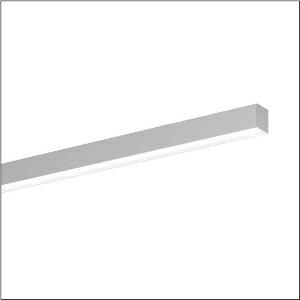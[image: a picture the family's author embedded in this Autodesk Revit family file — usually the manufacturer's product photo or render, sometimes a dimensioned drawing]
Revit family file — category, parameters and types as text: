
# Revit family: silica_r__21_51mx23db35sb_5652
name_source: partatom
category: Lighting Fixtures
units: mm (PartAtom-declared; Revit-internal decimal feet)

## family parameters
Cut with Voids When Loaded = No
Host = Face
Light Source = No
Part Type = Normal
Room Calculation Point = No
Round Connector Dimension = Use Diameter
Shared = No

## types (1)
- --- (1 x LED, 4100 lm, 30.1 W, 3000K)
    Apparent Load = 30 VA
    CIE Flux Codes = 78 96 99 100 100
    Color Rendering = 80
    Color Temperature = 3000K
    Default Elevation = 1800 mm
    Description = Silica® 21, office luminaire, primary optical cover: prismatic diffuser, of PMMA, CAT 2 (L<= 3000cd/m²), light emission: direct distribution, primary light characteristic: symmetric, installation type: surface-mounted, LED, rated luminous flux: 4.100lm, luminous efficacy: 136lm/W, light colour: 830, colour temperature: 3000K, with terminal, 3+2-pole, max. 2.5mm², mains connection: 220..240V, AC, 50/60Hz, rated input power: 30.1W, luminaire housing, of aluminium, metallic grey (RAL 9006), length: 1.504mm, width: 53mm, height: 53mm, protection rating (complete): IP20, insulation class (complete): insulation class I (protective earthing), certification: CE, permissible operating ambient temperature: 0..+35°C, standard: EN 50419, packaging unit: 1 piece
    Height = 0 mm  [stored 0 ft]
    Lamp = 1 x LED
    Lamp Light Flux = 4100 lm
    Lamp Power = 30.1 W
    Lamp count = 1
    Length = 1504 mm
    Luminous efficacy = 136 lm/W
    Manufacturer = Siteco
    ModVariant = No
    Model = 51MX23DB35SB
    Mounting Place = Ceiling
    Mounting Type = Recessed
    Number of Poles = 1
    OnlyDefault = Yes
    Power Factor = 1
    Product Name = Silica® 21
    Product group = office luminaire | ceiling recessed
    ProductGroupID = 401
    Protection Class = Protection class I
    Protection Degree = IP 20
    RLX_Detail_Level = 1
    RLX_Emergency_Light_Flux = 0 lm
    RLX_Emergency_Type = 0
    RLX_Emergency_Type_DB = No
    RlxData = <blob elided: 21189 chars, md5=ad9cbb13>
    Socket = socket
    Standby Power = 0 W
    System Light Flux = 4100 lm
    System Power = 30 W
    Type Comments = factory setting: luminous flux: 100 % | dim-lin: 254 | 345 mA
    Type Image = l_1313588.jpg
    URL = http://relux.com
    VarID = @adj_067813
    Voltage = 0 V
    Weight = 0.00 kg
    Width = 53 mm

note: [stored X ft] marks values corroborated as IEEE doubles in the binary element streams (Revit-internal decimal feet)

## geometry (parser evidence)
native form markers: Blend x4, Sweep x11
no freeform markers — native parametric forms only
